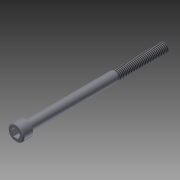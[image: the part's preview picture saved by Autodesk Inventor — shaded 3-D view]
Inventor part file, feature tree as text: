
AUTODESK INVENTOR PART (.ipt)
format: ipt  version: 2011 (Build 150239000, 239)  size: 94,208 bytes
history: native  units: in
note: dims shown in document units (in); Inventor stores cm internally (conversion verified against a paired STEP export)
features: extrude x3, sketch x3, chamfer x2, thread x1
ambient origin geometry x8: Origin, YZ Plane, XZ Plane, XY Plane, X Axis, Y Axis, Z Axis, Center Point
bodies: Solid1 (feature_tree)
feature tree (9):
  extrude  "Extrusion1"  Depth=0.19in TaperAngle=0.0deg
  extrude  "Extrusion2"  Depth=2.75in TaperAngle=0.0deg
  extrude  "Extrusion3"  Depth=0.125in TaperAngle=0.0deg
  thread  "Thread1"  [1 undecoded]
  chamfer  "Chamfer1"  Distance=0.02in Angle=45.0deg
  chamfer  "Chamfer2"  Distance=0.02in Angle=45.0deg
  sketch  "Sketch1"  dims[d0=0.312in d1=0.19in d2=0.0in]
  sketch  "Sketch2"  dims[d3=0.19in d4=2.75in d5=0.0in]
  sketch  "Sketch3"  dims[d6=0.1562in d7=0.125in d8=0.0in d9=1.0in d10=0.0in d11=0.02in d12=0.125in d13=45.0deg d14=0.02in d15=0.125in d16=45.0deg]
note: 1 required parameter value undecoded (feature->parameter linkage not recoverable at this tier; creation-order binding heuristic only, values carry confidence <= 0.55)
